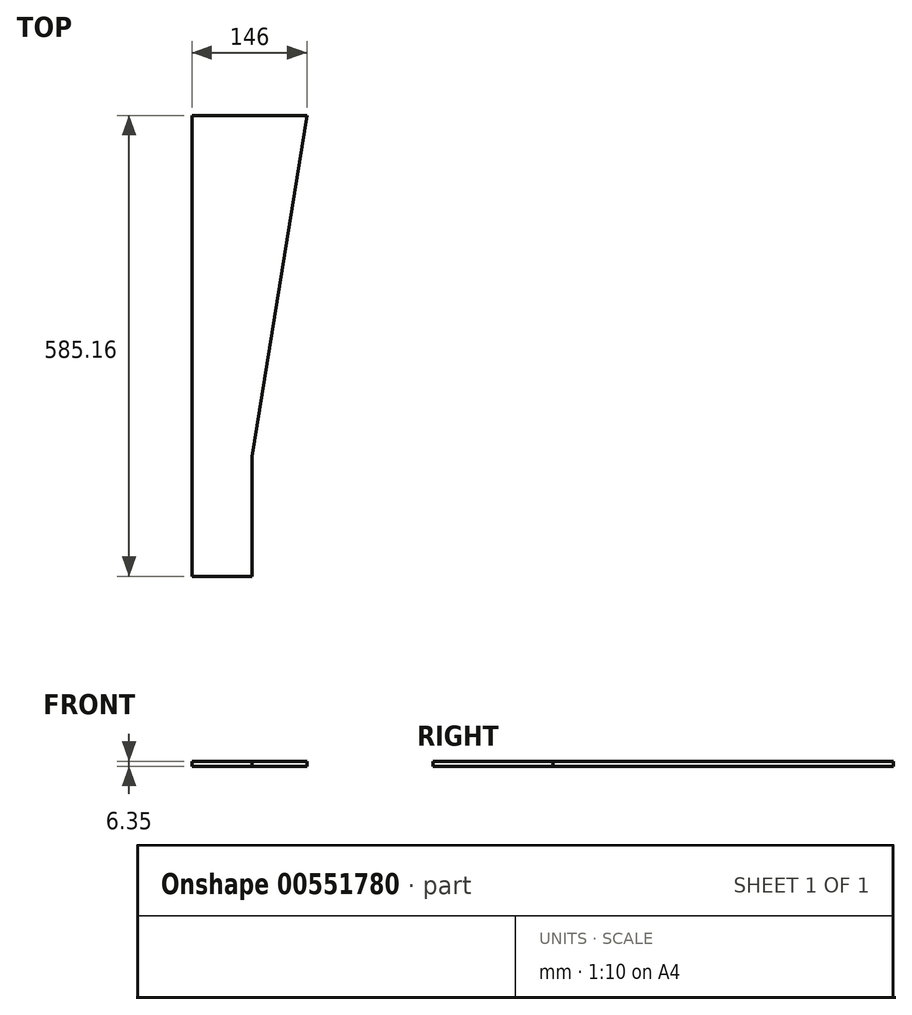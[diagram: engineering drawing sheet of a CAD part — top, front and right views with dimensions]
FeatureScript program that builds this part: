
annotation { "Feature Type Name" : "Feature", "Feature Type Description" : "" }
export const myFeature = defineFeature(function(context is Context, id is Id, definition is map)
    precondition{}
    {
        {
            var Q0;
            Q0=qCreatedBy(makeId("Top.planeOp"),FACE);
            var sketch = newSketch(context, id + "F0", { "sketchPlane" : qUnion([Q0])});
            skLineSegment(sketch, "E0.bottom", {"start": v(0, 0) * mm, "end": v(76.2, 0) * mm});
            skLineSegment(sketch, "E0.left", {"start": v(0, 0) * mm, "end": v(0, 152.4) * mm});
            skLineSegment(sketch, "E0.right", {"start": v(76.2, 0) * mm, "end": v(76.2, 152.4) * mm});
            skLineSegment(sketch, "E1", {"start": v(0, 152.4) * mm, "end": v(0, 585.16) * mm});
            skLineSegment(sketch, "E2", {"start": v(0, 585.16) * mm, "end": v(76.2, 585.16) * mm});
            skLineSegment(sketch, "E3", {"start": v(76.2, 152.4) * mm, "end": v(146, 585.16) * mm});
            skLineSegment(sketch, "E4", {"start": v(76.2, 585.16) * mm, "end": v(146, 585.16) * mm});
            skLineSegment(sketch, "E5", {"start": v(76.2, 585.16) * mm, "end": v(76.2, 152.4) * mm});
            skSolve(sketch);
        }
        {
            var Q0;
            Q0=makeQuery(id+"F0.imprint","IMPRINT",FACE,{"disambiguationData":[TD([[makeQuery(id+"F0.imprint","IMPRINT",EDGE,{"derivedFrom":sQuery(id+"F0.wireOp",EDGE,"E0.bottom")}),1.0]])]});
            var Q1;
            Q1=makeQuery(id+"F0.imprint","IMPRINT",FACE,{"disambiguationData":[TD([[makeQuery(id+"F0.imprint","IMPRINT",EDGE,{"derivedFrom":sQuery(id+"F0.wireOp",EDGE,"E3")}),1.0]])]});
            extrude(context, id + "F1", {"entities" : qUnion([Q0, Q1]), "depth" : 6.35 * mm, "offsetDistance" : 25.4 * mm});
        }
    });
